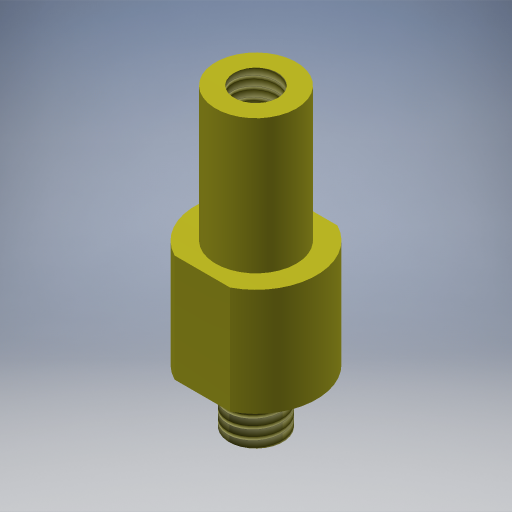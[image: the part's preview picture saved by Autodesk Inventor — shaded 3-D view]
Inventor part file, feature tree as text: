
AUTODESK INVENTOR PART (.ipt)
format: ipt  version: 2024.3 (Build 283343000, 343)  size: 287,232 bytes
history: native  units: mm
features: extrude x4, sketch x4, thread x1, hole x1, projected_geometry x1
ambient origin geometry x8: Origin, YZ Plane, XZ Plane, XY Plane, X Axis, Y Axis, Z Axis, Center Point
bodies: Volumenkörper1 (feature_tree)
feature tree (11):
  extrude  "Extrusion1"  Depth=8.0mm TaperAngle=0.0deg
  extrude  "Extrusion2"  Depth=4.0mm TaperAngle=0.0deg
  thread  "Gewinde1"  [1 undecoded]
  extrude  "Extrusion3"  Depth=10.0mm TaperAngle=0.0deg
  extrude  "Extrusion4"  Depth=10.0mm TaperAngle=0.0deg
  hole  "Bohrung1"  [1 undecoded]
  sketch  "Skizze2"  dims[d0=9.0mm d1=8.0mm d2=0.0mm]
  sketch  "Skizze3"  dims[d3=4.0mm d4=4.0mm d5=0.0mm d6=4.0mm d7=0.0mm]
  sketch  "Skizze4"  dims[d8=6.0mm d9=10.0mm d10=0.0mm]
  projected_geometry  "Projizierte Kontur1"
  sketch  "Skizze5"  dims[d11=8.0mm d12=10.0mm d13=0.0mm d14=3.242mm d15=8.0mm d16=4.0mm d17=2.0mm d18=90.0deg d19=11.8mm d20=20.594885mm]
note: 2 required parameter values undecoded (feature->parameter linkage not recoverable at this tier; creation-order binding heuristic only, values carry confidence <= 0.55)
